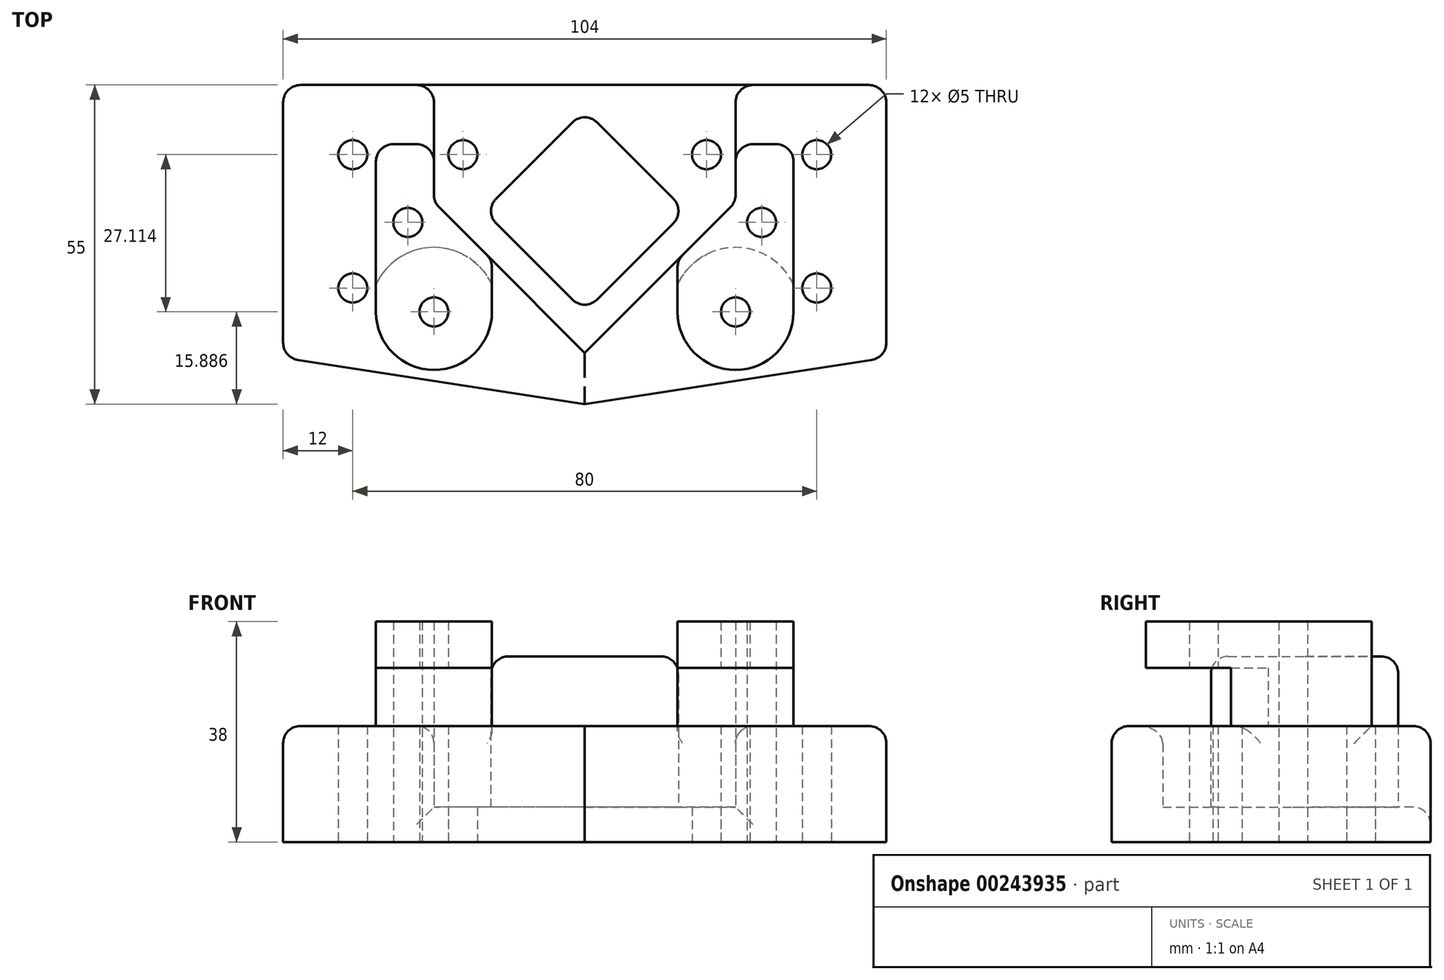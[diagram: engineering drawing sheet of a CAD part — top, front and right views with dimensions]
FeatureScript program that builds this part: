
annotation { "Feature Type Name" : "Feature", "Feature Type Description" : "" }
export const myFeature = defineFeature(function(context is Context, id is Id, definition is map)
    precondition{}
    {
        {
            var Q0;
            Q0=qCreatedBy(makeId("Top.planeOp"),FACE);
            var sketch = newSketch(context, id + "F0", { "sketchPlane" : qUnion([Q0])});
            skLineSegment(sketch, "E0", {"start": v(0, 0) * mm, "end": v(52, 0) * mm});
            skLineSegment(sketch, "E1", {"start": v(0, 0) * mm, "end": v(-52, 0) * mm});
            skLineSegment(sketch, "E2", {"start": v(0, 0) * mm, "end": v(0, -55) * mm, "construction": true});
            skLineSegment(sketch, "E3", {"start": v(-52, 0) * mm, "end": v(-52, -47) * mm});
            skLineSegment(sketch, "E4", {"start": v(52, 0) * mm, "end": v(52, -47) * mm});
            skLineSegment(sketch, "E5", {"start": v(0, -4.32) * mm, "end": v(-17.4, -21.72) * mm});
            skLineSegment(sketch, "E6", {"start": v(17.4, -21.72) * mm, "end": v(0, -4.32) * mm});
            skLineSegment(sketch, "E7.0", {"start": v(0, -12) * mm, "end": v(-21, -12) * mm, "construction": true});
            skLineSegment(sketch, "E8.0", {"start": v(0, -12) * mm, "end": v(21, -12) * mm, "construction": true});
            skLineSegment(sketch, "E9.0", {"start": v(-40, 0) * mm, "end": v(-40, -14.5) * mm, "construction": true});
            skLineSegment(sketch, "E10.0", {"start": v(40, 0) * mm, "end": v(40, -14.5) * mm, "construction": true});
            skLineSegment(sketch, "E11", {"start": v(-52, -47) * mm, "end": v(52, -47) * mm, "construction": true});
            skLineSegment(sketch, "E12.0", {"start": v(-52, -35) * mm, "end": v(52, -35) * mm, "construction": true});
            skLineSegment(sketch, "E13.0", {"start": v(-18, -12) * mm, "end": v(-18, -35) * mm, "construction": true});
            skLineSegment(sketch, "E14.0", {"start": v(18, -12) * mm, "end": v(18, -35) * mm, "construction": true});
            skLineSegment(sketch, "E15.trimOffspring", {"start": v(-31.5, -12) * mm, "end": v(-40, -12) * mm, "construction": true});
            skLineSegment(sketch, "E16.trimOffspring", {"start": v(31.5, -12) * mm, "end": v(40, -12) * mm, "construction": true});
            skLineSegment(sketch, "E17.trimOffspring", {"start": v(-40, -20.5) * mm, "end": v(-40, -35) * mm, "construction": true});
            skLineSegment(sketch, "E18.trimOffspring", {"start": v(40, -20.5) * mm, "end": v(40, -35) * mm, "construction": true});
            skLineSegment(sketch, "E19.0", {"start": v(0, -39.11) * mm, "end": v(-17.4, -21.72) * mm});
            skLineSegment(sketch, "E20.0", {"start": v(0, -39.11) * mm, "end": v(17.4, -21.72) * mm});
            skLineSegment(sketch, "E21.0", {"start": v(-26, 0) * mm, "end": v(-26, -20.19) * mm});
            skLineSegment(sketch, "E22.0", {"start": v(26, 0) * mm, "end": v(26, -20.19) * mm});
            skLineSegment(sketch, "E23", {"start": v(0, -39.11) * mm, "end": v(-36, -39.11) * mm, "construction": true});
            skLineSegment(sketch, "E24", {"start": v(0, -39.11) * mm, "end": v(36, -39.11) * mm, "construction": true});
            skLineSegment(sketch, "E25.0", {"start": v(0, -46.19) * mm, "end": v(26, -20.19) * mm});
            skLineSegment(sketch, "E26.0", {"start": v(0, -46.19) * mm, "end": v(-26, -20.19) * mm});
            skLineSegment(sketch, "E27.trimOffspring", {"start": v(-26, -35) * mm, "end": v(-26, -39.11) * mm, "construction": true});
            skLineSegment(sketch, "E28.trimOffspring", {"start": v(26, -35) * mm, "end": v(26, -39.11) * mm, "construction": true});
            skCircle(sketch, "E29", {"center": v(-21, -12) * mm, "radius": 2.5 * mm});
            skCircle(sketch, "E30", {"center": v(21, -12) * mm, "radius": 2.5 * mm});
            skCircle(sketch, "E31", {"center": v(-40, -12) * mm, "radius": 2.5 * mm});
            skCircle(sketch, "E32", {"center": v(-40, -35) * mm, "radius": 2.5 * mm});
            skCircle(sketch, "E33", {"center": v(40, -35) * mm, "radius": 2.5 * mm});
            skCircle(sketch, "E34", {"center": v(40, -12) * mm, "radius": 2.5 * mm});
            skLineSegment(sketch, "E35.0", {"start": v(-35.36, -55) * mm, "end": v(35.36, -55) * mm, "construction": true});
            skLineSegment(sketch, "E36", {"start": v(-52, -47) * mm, "end": v(0, -55) * mm});
            skLineSegment(sketch, "E37", {"start": v(52, -47) * mm, "end": v(0, -55) * mm});
            skCircle(sketch, "E38", {"center": v(-26, -39.11) * mm, "radius": 2.5 * mm});
            skCircle(sketch, "E39", {"center": v(26, -39.11) * mm, "radius": 2.5 * mm});
            skLineSegment(sketch, "E40.0", {"start": v(-16, -30.19) * mm, "end": v(-16, -39.11) * mm});
            skLineSegment(sketch, "E41.0", {"start": v(16, -30.19) * mm, "end": v(16, -39.11) * mm});
            skPoint(sketch, "E42.orphan", {"position": v(52, -46.19) * mm});
            skPoint(sketch, "E43.orphan", {"position": v(-52, -46.19) * mm});
            skArc(sketch, "E44", {"start": v(-36, -39.11) * mm, "mid": v(-26, -49.11) * mm, "end": v(-16, -39.11) * mm});
            skArc(sketch, "E45", {"start": v(16, -39.11) * mm, "mid": v(26, -49.11) * mm, "end": v(36, -39.11) * mm});
            skLineSegment(sketch, "E46", {"start": v(-36, -39.11) * mm, "end": v(-36, -10.19) * mm});
            skLineSegment(sketch, "E47", {"start": v(36, -39.11) * mm, "end": v(36, -10.19) * mm});
            skLineSegment(sketch, "E48", {"start": v(-36, -10.19) * mm, "end": v(-26, -10.19) * mm});
            skLineSegment(sketch, "E49.trimOffspring", {"start": v(26, -10.19) * mm, "end": v(36, -10.19) * mm});
            skLineSegment(sketch, "E50", {"start": v(-26, -20.19) * mm, "end": v(-30.5, -20.19) * mm, "construction": true});
            skLineSegment(sketch, "E51", {"start": v(-30.5, -20.19) * mm, "end": v(-30.5, -23.69) * mm, "construction": true});
            skLineSegment(sketch, "E52.MirrorCS", {"start": v(26, -20.19) * mm, "end": v(30.5, -20.19) * mm, "construction": true});
            skLineSegment(sketch, "E53.MirrorCS", {"start": v(30.5, -20.19) * mm, "end": v(30.5, -23.69) * mm, "construction": true});
            skCircle(sketch, "E54", {"center": v(-30.5, -23.69) * mm, "radius": 2.5 * mm});
            skCircle(sketch, "E55", {"center": v(30.5, -23.69) * mm, "radius": 2.5 * mm});
            skSolve(sketch);
        }
        {
            var Q0;
            Q0=qCreatedBy(makeId("Top.planeOp"),FACE);
            cPlane(context, id + "F1", {"entities" : qUnion([Q0]), "cplaneType" : CPlaneType.OFFSET, "offset" : 20 * mm, "width" : 150 * mm, "height" : 150 * mm});
        }
        {
            var Q0;
            Q0=qCreatedBy(id+"F1.planeOp",FACE);
            var sketch = newSketch(context, id + "F2", { "sketchPlane" : qUnion([Q0])});
            skLineSegment(sketch, "E56", {"start": v(0, 0) * mm, "end": v(-26, 0) * mm, "construction": true});
            skLineSegment(sketch, "E57", {"start": v(-26, 0) * mm, "end": v(-26, -39) * mm, "construction": true});
            skLineSegment(sketch, "E58", {"start": v(0, 0) * mm, "end": v(26, 0) * mm, "construction": true});
            skLineSegment(sketch, "E59", {"start": v(26, 0) * mm, "end": v(26, -39) * mm, "construction": true});
            skCircle(sketch, "E60", {"center": v(-26, -39) * mm, "radius": 11 * mm});
            skCircle(sketch, "E61", {"center": v(26, -39) * mm, "radius": 11 * mm});
            skSolve(sketch);
        }
        {
            var Q0;
            Q0=makeQuery(id+"F0.imprint","IMPRINT",FACE,{"disambiguationData":[TD([[makeQuery(id+"F0.imprint","IMPRINT",EDGE,{"derivedFrom":sQuery(id+"F0.wireOp",EDGE,"E5")}),1.0]])]});
            extrude(context, id + "F3", {"entities" : qUnion([Q0]), "depth" : 32 * mm, "offsetDistance" : 25 * mm});
        }
        {
            var Q0;
            Q0=makeQuery(id+"F0.imprint","IMPRINT",FACE,{"disambiguationData":[TD([[makeQuery(id+"F0.imprint","IMPRINT",EDGE,{"derivedFrom":sQuery(id+"F0.wireOp",EDGE,"E5")}),-1.0]])]});
            extrude(context, id + "F4", {"entities" : qUnion([Q0]), "operationType" : NewBodyOperationType.ADD, "depth" : 6 * mm, "offsetDistance" : 25 * mm});
        }
        {
            var Q0;
            {var subQ13=sQuery(id+"F0.wireOp",EDGE,"E3");Q0=makeQuery(id+"F0.imprint","IMPRINT",FACE,{"disambiguationData":[TD([[makeQuery(id+"F0.imprint","IMPRINT",EDGE,{"derivedFrom":subQ13}),1.0]])]});}
            extrude(context, id + "F5", {"entities" : qUnion([Q0]), "operationType" : NewBodyOperationType.ADD, "depth" : 20 * mm, "offsetDistance" : 25 * mm});
        }
        {
            var Q0;
            Q0=makeQuery(id+"F0.imprint","IMPRINT",FACE,{"disambiguationData":[TD([[makeQuery(id+"F0.imprint","IMPRINT",EDGE,{"derivedFrom":sQuery(id+"F0.wireOp",EDGE,"E38")}),-1.0]])]});
            var Q1;
            Q1=makeQuery(id+"F0.imprint","IMPRINT",FACE,{"disambiguationData":[TD([[makeQuery(id+"F0.imprint","IMPRINT",EDGE,{"derivedFrom":sQuery(id+"F0.wireOp",EDGE,"E39")}),-1.0]])]});
            extrude(context, id + "F6", {"entities" : qUnion([Q0, Q1]), "operationType" : NewBodyOperationType.ADD, "depth" : 38 * mm, "offsetDistance" : 25 * mm});
        }
        {
            var Q0;
            Q0=makeQuery(id+"F2.imprint","IMPRINT",FACE,{"disambiguationData":[TD([[makeQuery(id+"F2.imprint","IMPRINT",EDGE,{"derivedFrom":sQuery(id+"F2.wireOp",EDGE,"E60")}),1.0]])]});
            var Q1;
            Q1=makeQuery(id+"F2.imprint","IMPRINT",FACE,{"disambiguationData":[TD([[makeQuery(id+"F2.imprint","IMPRINT",EDGE,{"derivedFrom":sQuery(id+"F2.wireOp",EDGE,"E61")}),1.0]])]});
            extrude(context, id + "F7", {"entities" : qUnion([Q0, Q1]), "operationType" : NewBodyOperationType.REMOVE, "depth" : 10 * mm, "offsetDistance" : 25 * mm});
        }
        {
            var Q0;
            Q0=makeQuery(id+"F3.opExtrude","CAP_EDGE",EDGE,{"disambiguationData":[OSD([sQuery(id+"F0.wireOp",EDGE,"E19.0")])],"isStart":false});
            var Q1;
            Q1=makeQuery(id+"F3.opExtrude","CAP_FACE",FACE,{"disambiguationData":[OSD([sQuery(id+"F0.wireOp",EDGE,"E5"),sQuery(id+"F0.wireOp",EDGE,"E6"),sQuery(id+"F0.wireOp",EDGE,"E19.0"),sQuery(id+"F0.wireOp",EDGE,"E20.0")])],"isStart":false});
            var Q2;
            Q2=makeQuery(id+"F3.opExtrude","SWEPT_EDGE",EDGE,{"disambiguationData":[OSD([sQuery(id+"F0.wireOp",EDGE,"E19.0"),sQuery(id+"F0.wireOp",EDGE,"E20.0")])]});
            var Q3;
            Q3=makeQuery(id+"F3.opExtrude","SWEPT_EDGE",EDGE,{"disambiguationData":[OSD([sQuery(id+"F0.wireOp",EDGE,"E6"),sQuery(id+"F0.wireOp",EDGE,"E20.0")])]});
            var Q4;
            Q4=makeQuery(id+"F3.opExtrude","SWEPT_EDGE",EDGE,{"disambiguationData":[OSD([sQuery(id+"F0.wireOp",EDGE,"E5"),sQuery(id+"F0.wireOp",EDGE,"E6")])]});
            var Q5;
            Q5=makeQuery(id+"F3.opExtrude","SWEPT_EDGE",EDGE,{"disambiguationData":[OSD([sQuery(id+"F0.wireOp",EDGE,"E5"),sQuery(id+"F0.wireOp",EDGE,"E19.0")])]});
            var Q6;
            Q6=makeQuery(id+"F5.opExtrude","CAP_EDGE",EDGE,{"disambiguationData":[OSD([sQuery(id+"F0.wireOp",EDGE,"E25.0")])],"isStart":false});
            var Q7;
            Q7=makeQuery(id+"F5.opExtrude","CAP_EDGE",EDGE,{"disambiguationData":[OSD([sQuery(id+"F0.wireOp",EDGE,"E26.0")])],"isStart":false});
            var Q8;
            Q8=makeQuery(id+"F6.opExtrude","SWEPT_EDGE",EDGE,{"disambiguationData":[OSD([sQuery(id+"F0.wireOp",EDGE,"E25.0"),sQuery(id+"F0.wireOp",EDGE,"E41.0")])]});
            var Q9;
            Q9=makeQuery(id+"F6.opExtrude","SWEPT_EDGE",EDGE,{"disambiguationData":[OSD([sQuery(id+"F0.wireOp",EDGE,"E26.0"),sQuery(id+"F0.wireOp",EDGE,"E40.0")])]});
            var Q10;
            Q10=makeQuery(id+"F6.opExtrude","SWEPT_EDGE",EDGE,{"disambiguationData":[OSD([sQuery(id+"F0.wireOp",EDGE,"E21.0"),sQuery(id+"F0.wireOp",EDGE,"E26.0")])]});
            var Q11;
            Q11=makeQuery(id+"F6.opExtrude","SWEPT_EDGE",EDGE,{"disambiguationData":[OSD([sQuery(id+"F0.wireOp",EDGE,"E21.0"),sQuery(id+"F0.wireOp",EDGE,"E48")])]});
            var Q12;
            Q12=makeQuery(id+"F6.opExtrude","SWEPT_EDGE",EDGE,{"disambiguationData":[OSD([sQuery(id+"F0.wireOp",EDGE,"E22.0"),sQuery(id+"F0.wireOp",EDGE,"E25.0")])]});
            var Q13;
            Q13=makeQuery(id+"F6.opExtrude","SWEPT_EDGE",EDGE,{"disambiguationData":[OSD([sQuery(id+"F0.wireOp",EDGE,"E22.0"),sQuery(id+"F0.wireOp",EDGE,"E49.trimOffspring")])]});
            var Q14;
            Q14=makeQuery(id+"F5.opExtrude","SWEPT_EDGE",EDGE,{"disambiguationData":[OSD([sQuery(id+"F0.wireOp",EDGE,"E0"),sQuery(id+"F0.wireOp",EDGE,"E22.0")])]});
            var Q15;
            Q15=makeQuery(id+"F6.opExtrude","SWEPT_EDGE",EDGE,{"disambiguationData":[OSD([sQuery(id+"F0.wireOp",EDGE,"E46"),sQuery(id+"F0.wireOp",EDGE,"E48")])]});
            var Q16;
            Q16=makeQuery(id+"F5.opExtrude","SWEPT_EDGE",EDGE,{"disambiguationData":[OSD([sQuery(id+"F0.wireOp",EDGE,"E1"),sQuery(id+"F0.wireOp",EDGE,"E3")])]});
            var Q17;
            Q17=makeQuery(id+"F5.opExtrude","SWEPT_EDGE",EDGE,{"disambiguationData":[OSD([sQuery(id+"F0.wireOp",EDGE,"E3"),sQuery(id+"F0.wireOp",EDGE,"E36")])]});
            var Q18;
            Q18=makeQuery(id+"F6.opExtrude","SWEPT_EDGE",EDGE,{"disambiguationData":[OSD([sQuery(id+"F0.wireOp",EDGE,"E47"),sQuery(id+"F0.wireOp",EDGE,"E49.trimOffspring")])]});
            var Q19;
            Q19=makeQuery(id+"F5.opExtrude","SWEPT_EDGE",EDGE,{"disambiguationData":[OSD([sQuery(id+"F0.wireOp",EDGE,"E0"),sQuery(id+"F0.wireOp",EDGE,"E4")])]});
            var Q20;
            Q20=makeQuery(id+"F5.opExtrude","SWEPT_EDGE",EDGE,{"disambiguationData":[OSD([sQuery(id+"F0.wireOp",EDGE,"E4"),sQuery(id+"F0.wireOp",EDGE,"E37")])]});
            var Q21;
            Q21=makeQuery(id+"F5.opExtrude","SWEPT_EDGE",EDGE,{"disambiguationData":[OSD([sQuery(id+"F0.wireOp",EDGE,"E1"),sQuery(id+"F0.wireOp",EDGE,"E21.0")])]});
            var Q22;
            Q22=makeQuery(id+"F5.opExtrude","CAP_EDGE",EDGE,{"disambiguationData":[OSD([sQuery(id+"F0.wireOp",EDGE,"E22.0")])],"isStart":false});
            var Q23;
            Q23=makeQuery(id+"F5.opExtrude","CAP_EDGE",EDGE,{"disambiguationData":[OSD([sQuery(id+"F0.wireOp",EDGE,"E0")])],"isStart":false});
            var Q24;
            Q24=makeQuery(id+"F5.opExtrude","CAP_EDGE",EDGE,{"disambiguationData":[OSD([sQuery(id+"F0.wireOp",EDGE,"E4")])],"isStart":false});
            var Q25;
            Q25=makeQuery(id+"F5.opExtrude","CAP_EDGE",EDGE,{"disambiguationData":[OSD([sQuery(id+"F0.wireOp",EDGE,"E37")])],"isStart":false});
            var Q26;
            Q26=makeQuery(id+"F5.opExtrude","CAP_EDGE",EDGE,{"disambiguationData":[OSD([sQuery(id+"F0.wireOp",EDGE,"E36")])],"isStart":false});
            var Q27;
            Q27=makeQuery(id+"F5.opExtrude","CAP_EDGE",EDGE,{"disambiguationData":[OSD([sQuery(id+"F0.wireOp",EDGE,"E3")])],"isStart":false});
            var Q28;
            Q28=makeQuery(id+"F5.opExtrude","CAP_EDGE",EDGE,{"disambiguationData":[OSD([sQuery(id+"F0.wireOp",EDGE,"E21.0")])],"isStart":false});
            var Q29;
            Q29=makeQuery(id+"F5.opExtrude","CAP_EDGE",EDGE,{"disambiguationData":[OSD([sQuery(id+"F0.wireOp",EDGE,"E1")])],"isStart":false});
            var Q30;
            Q30=makeQuery(id+"F4.opExtrude","CAP_EDGE",EDGE,{"disambiguationData":[OSD([sQuery(id+"F0.wireOp",EDGE,"E0"),sQuery(id+"F0.wireOp",EDGE,"E1")])],"isStart":false});
            fillet(context, id + "F8", {"entities" : qUnion([Q0, Q1, Q2, Q3, Q4, Q5, Q6, Q7, Q8, Q9, Q10, Q11, Q12, Q13, Q14, Q15, Q16, Q17, Q18, Q19, Q20, Q21, Q22, Q23, Q24, Q25, Q26, Q27, Q28, Q29, Q30]), "radius" : 3 * mm, "tangentPropagation" : true, "allowEdgeOverflow" : false});
        }
    });
